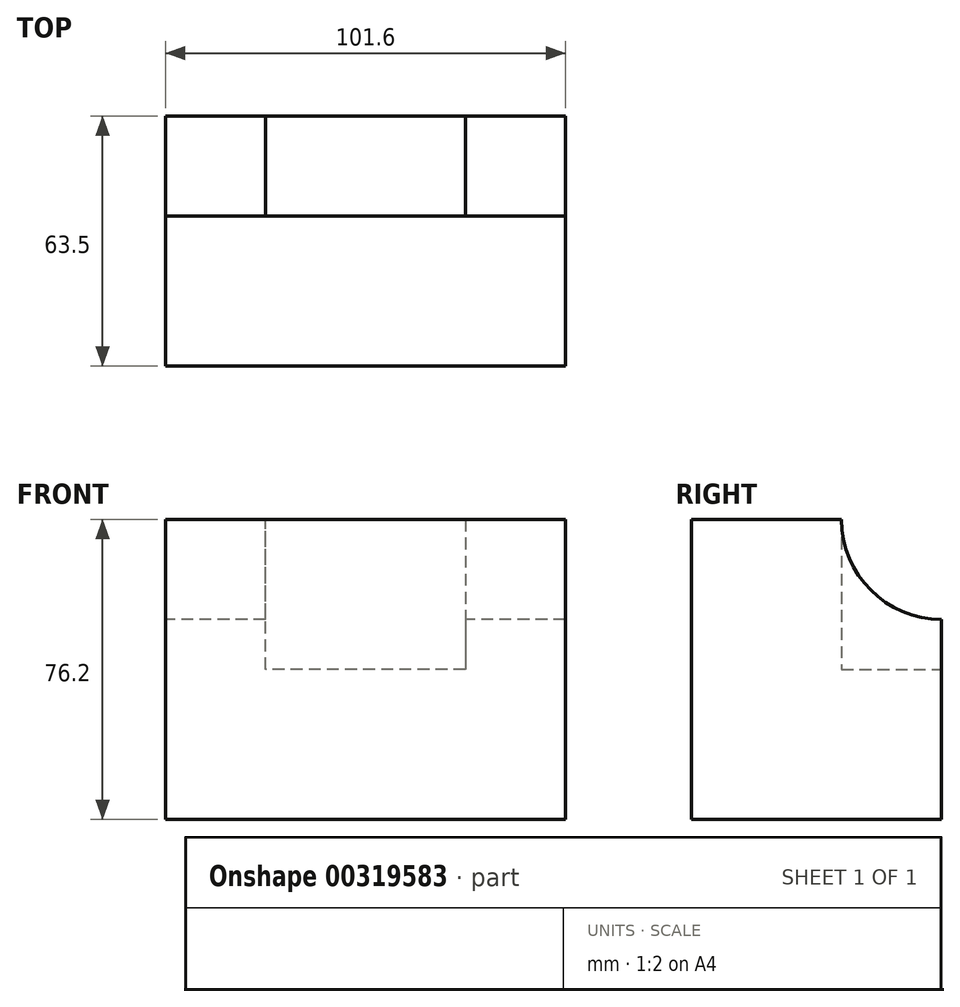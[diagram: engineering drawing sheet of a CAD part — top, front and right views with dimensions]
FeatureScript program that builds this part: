
annotation { "Feature Type Name" : "Feature", "Feature Type Description" : "" }
export const myFeature = defineFeature(function(context is Context, id is Id, definition is map)
    precondition{}
    {
        {
            var Q0;
            Q0=qCreatedBy(makeId("Front.planeOp"),FACE);
            var sketch = newSketch(context, id + "F0", { "sketchPlane" : qUnion([Q0])});
            skLineSegment(sketch, "E0", {"start": v(-41.51, -55.66) * mm, "end": v(60.09, -55.66) * mm});
            skLineSegment(sketch, "E1", {"start": v(60.09, -55.66) * mm, "end": v(60.09, 20.54) * mm});
            skLineSegment(sketch, "E2", {"start": v(60.09, 20.54) * mm, "end": v(-41.51, 20.54) * mm});
            skLineSegment(sketch, "E3", {"start": v(-41.51, 20.54) * mm, "end": v(-41.51, -55.66) * mm});
            skSolve(sketch);
        }
        {
            var Q0;
            Q0=makeQuery(id+"F0.imprint","IMPRINT",FACE,{"disambiguationData":[TD([[makeQuery(id+"F0.imprint","IMPRINT",EDGE,{"derivedFrom":sQuery(id+"F0.wireOp",EDGE,"E0")}),1.0]])]});
            extrude(context, id + "F1", {"entities" : qUnion([Q0]), "depth" : 63.5 * mm});
        }
        {
            var Q0;
            Q0=makeQuery(id+"F1.opExtrude","CAP_FACE",FACE,{"disambiguationData":[OSD([sQuery(id+"F0.wireOp",EDGE,"E0"),sQuery(id+"F0.wireOp",EDGE,"E1"),sQuery(id+"F0.wireOp",EDGE,"E2"),sQuery(id+"F0.wireOp",EDGE,"E3")])],"isStart":true});
            var sketch = newSketch(context, id + "F2", { "sketchPlane" : qUnion([Q0])});
            skLineSegment(sketch, "E4", {"start": v(-34.69, 20.54) * mm, "end": v(-34.69, -17.56) * mm});
            skLineSegment(sketch, "E5", {"start": v(-34.69, -17.56) * mm, "end": v(16.11, -17.56) * mm});
            skLineSegment(sketch, "E6", {"start": v(16.11, -17.56) * mm, "end": v(16.11, 20.54) * mm});
            skLineSegment(sketch, "E7", {"start": v(16.11, 20.54) * mm, "end": v(-34.69, 20.54) * mm});
            skSolve(sketch);
        }
        {
            var Q0;
            Q0=makeQuery(id+"F2.imprint","IMPRINT",FACE,{"disambiguationData":[TD([[makeQuery(id+"F2.imprint","IMPRINT",EDGE,{"derivedFrom":sQuery(id+"F2.wireOp",EDGE,"E4")}),1.0]])]});
            extrude(context, id + "F3", {"entities" : qUnion([Q0]), "operationType" : NewBodyOperationType.REMOVE, "oppositeDirection" : true, "depth" : 25.4 * mm});
        }
        {
            var Q0;
            Q0=makeQuery(id+"F1.opExtrude","SWEPT_FACE",FACE,{"disambiguationData":[OSD([sQuery(id+"F0.wireOp",EDGE,"E3")])]});
            var sketch = newSketch(context, id + "F4", { "sketchPlane" : qUnion([Q0])});
            skArc(sketch, "E8", {"start": v(0, -4.86) * mm, "mid": v(17.96, 2.58) * mm, "end": v(25.4, 20.54) * mm});
            skLineSegment(sketch, "E9", {"start": v(25.4, 20.54) * mm, "end": v(0, 20.54) * mm});
            skLineSegment(sketch, "E10", {"start": v(0, 20.54) * mm, "end": v(0, -4.86) * mm});
            skSolve(sketch);
        }
        {
            var Q0;
            Q0=makeQuery(id+"F4.imprint","IMPRINT",FACE,{"disambiguationData":[TD([[makeQuery(id+"F4.imprint","IMPRINT",EDGE,{"derivedFrom":sQuery(id+"F4.wireOp",EDGE,"E8")}),1.0]])]});
            extrude(context, id + "F5", {"entities" : qUnion([Q0]), "operationType" : NewBodyOperationType.REMOVE, "endBound" : BoundingType.THROUGH_ALL, "oppositeDirection" : true, "depth" : 25.4 * mm});
        }
    });
